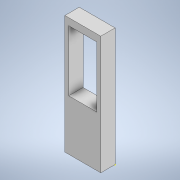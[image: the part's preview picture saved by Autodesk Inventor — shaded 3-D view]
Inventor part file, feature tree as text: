
AUTODESK INVENTOR PART (.ipt)
format: ipt  version: 2021.2 (Build 252289000, 289)  size: 126,464 bytes
history: native  units: in
note: dims shown in document units (in); Inventor stores cm internally (conversion verified against a paired STEP export)
features: sketch x4, extrude x3
ambient origin geometry x8: Origin, YZ Plane, XZ Plane, XY Plane, X Axis, Y Axis, Z Axis, Center Point
bodies: Solid1 (feature_tree)
feature tree (7):
  extrude  "Extrusion1"  Depth=3.0in
  sketch  "Sketch2"  dims[d14=0.3937in d15=0.3937in]
  extrude  "Extrusion2"  Depth=0.3937in
  extrude  "Extrusion3"  Depth=0.7874in
  sketch  "Sketch1"  dims[d0=1.0in d1=3.0in]
  sketch  "Sketch3"  dims[d16=0.7874in d17=1.5866in]
  sketch  "Sketch4"  dims[d18=0.4in d19=0.0in d20=0.3in d21=0.0in d22=0.8in d23=0.0in]
